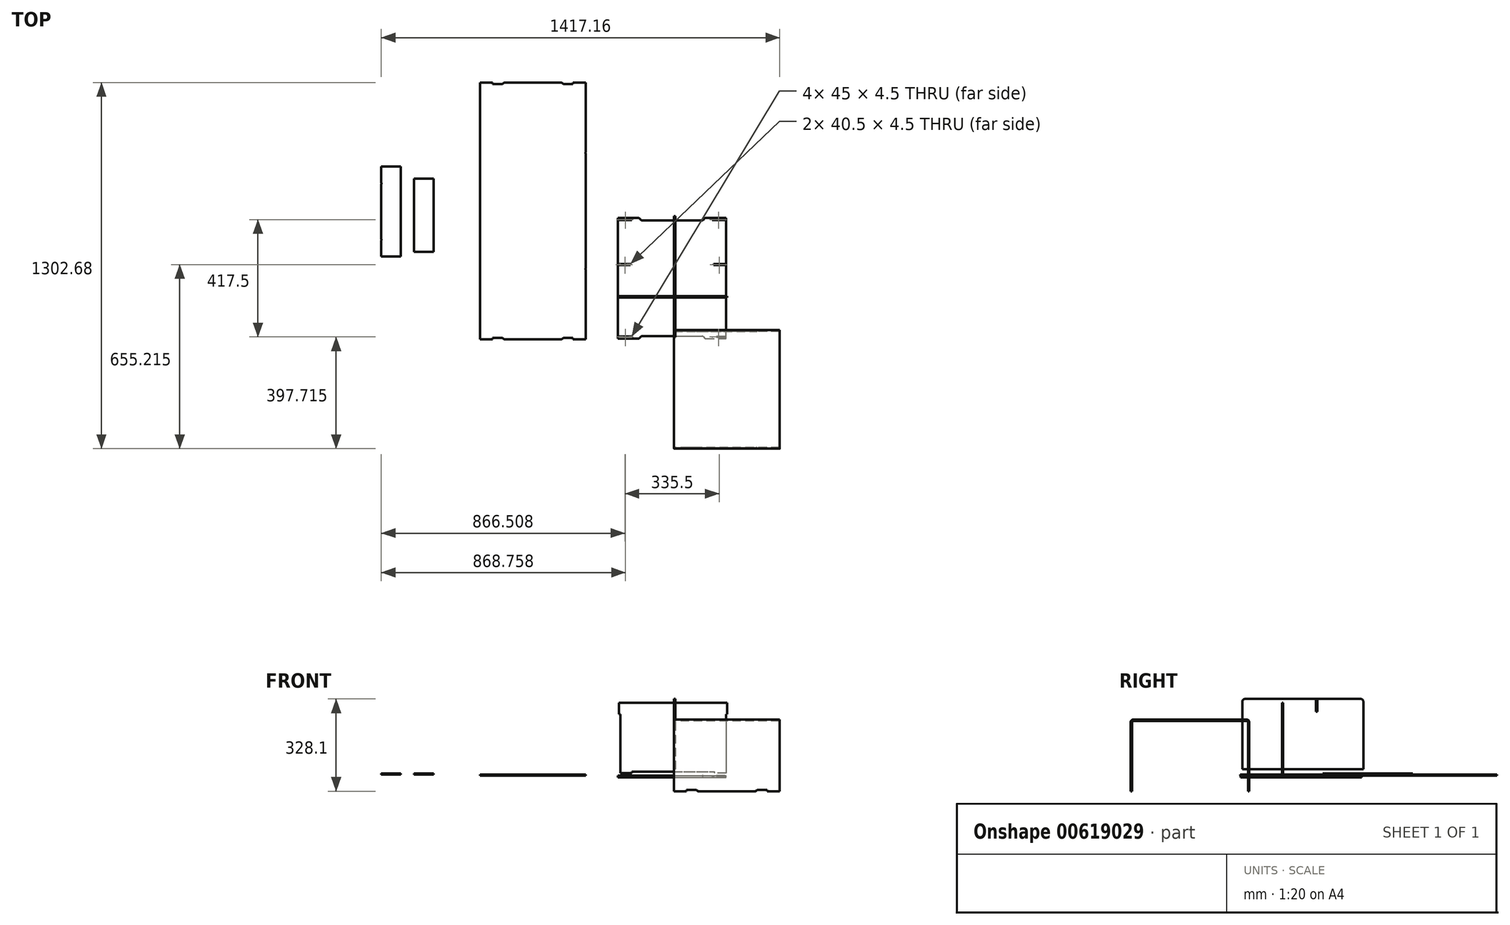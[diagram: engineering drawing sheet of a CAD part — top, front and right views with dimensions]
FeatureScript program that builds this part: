
annotation { "Feature Type Name" : "Feature", "Feature Type Description" : "" }
export const myFeature = defineFeature(function(context is Context, id is Id, definition is map)
    precondition{}
    {
        {
            var Q0;
            Q0=qCreatedBy(makeId("Top.planeOp"),FACE);
            var sketch = newSketch(context, id + "F0", { "sketchPlane" : qUnion([Q0])});
            skLineSegment(sketch, "E0.bottom", {"start": v(-199.4, -151.06) * mm, "end": v(-126.97, -151.06) * mm});
            skLineSegment(sketch, "E0.top", {"start": v(-199.4, 278.94) * mm, "end": v(-126.97, 278.94) * mm});
            skLineSegment(sketch, "E0.left", {"start": v(-199.4, -151.06) * mm, "end": v(-199.4, 110.44) * mm});
            skLineSegment(sketch, "E0.right", {"start": v(185.6, -151.06) * mm, "end": v(185.6, 110.44) * mm});
            skLineSegment(sketch, "E1", {"start": v(-194.9, 114.94) * mm, "end": v(-154.4, 114.94) * mm});
            skLineSegment(sketch, "E2", {"start": v(-154.4, 114.94) * mm, "end": v(-154.4, 110.44) * mm});
            skLineSegment(sketch, "E3", {"start": v(-154.4, 110.44) * mm, "end": v(-194.9, 110.44) * mm});
            skLineSegment(sketch, "E4", {"start": v(181.1, 114.94) * mm, "end": v(140.6, 114.94) * mm});
            skLineSegment(sketch, "E5", {"start": v(140.6, 114.94) * mm, "end": v(140.6, 110.44) * mm});
            skLineSegment(sketch, "E6", {"start": v(140.6, 110.44) * mm, "end": v(181.1, 110.44) * mm});
            skLineSegment(sketch, "E7.trimOffspring", {"start": v(-199.4, 114.94) * mm, "end": v(-199.4, 278.94) * mm});
            skLineSegment(sketch, "E8.trimOffspring", {"start": v(185.6, 114.94) * mm, "end": v(185.6, 278.94) * mm});
            skLineSegment(sketch, "E9", {"start": v(-199.4, 114.94) * mm, "end": v(-199.4, 110.44) * mm});
            skLineSegment(sketch, "E10", {"start": v(-194.9, 114.94) * mm, "end": v(-194.9, 110.44) * mm});
            skLineSegment(sketch, "E11", {"start": v(185.6, 114.94) * mm, "end": v(185.6, 110.44) * mm});
            skLineSegment(sketch, "E12", {"start": v(181.1, 114.94) * mm, "end": v(181.1, 110.44) * mm});
            skLineSegment(sketch, "E13.bottom", {"start": v(-194.9, -142.56) * mm, "end": v(-149.9, -142.56) * mm});
            skLineSegment(sketch, "E13.top", {"start": v(-194.9, -147.06) * mm, "end": v(-149.9, -147.06) * mm});
            skLineSegment(sketch, "E13.left", {"start": v(-194.9, -142.56) * mm, "end": v(-194.9, -147.06) * mm});
            skLineSegment(sketch, "E13.right", {"start": v(-149.9, -142.56) * mm, "end": v(-149.9, -147.06) * mm});
            skLineSegment(sketch, "E14.bottom", {"start": v(181.1, -142.56) * mm, "end": v(136.1, -142.56) * mm});
            skLineSegment(sketch, "E14.top", {"start": v(181.1, -147.06) * mm, "end": v(136.1, -147.06) * mm});
            skLineSegment(sketch, "E14.left", {"start": v(181.1, -142.56) * mm, "end": v(181.1, -147.06) * mm});
            skLineSegment(sketch, "E14.right", {"start": v(136.1, -142.56) * mm, "end": v(136.1, -147.06) * mm});
            skLineSegment(sketch, "E15.bottom", {"start": v(-194.9, 274.94) * mm, "end": v(-149.9, 274.94) * mm});
            skLineSegment(sketch, "E15.top", {"start": v(-194.9, 270.44) * mm, "end": v(-149.9, 270.44) * mm});
            skLineSegment(sketch, "E15.left", {"start": v(-194.9, 274.94) * mm, "end": v(-194.9, 270.44) * mm});
            skLineSegment(sketch, "E15.right", {"start": v(-149.9, 274.94) * mm, "end": v(-149.9, 270.44) * mm});
            skLineSegment(sketch, "E16.bottom", {"start": v(181.1, 274.94) * mm, "end": v(136.1, 274.94) * mm});
            skLineSegment(sketch, "E16.top", {"start": v(181.1, 270.44) * mm, "end": v(136.1, 270.44) * mm});
            skLineSegment(sketch, "E16.left", {"start": v(181.1, 274.94) * mm, "end": v(181.1, 270.44) * mm});
            skLineSegment(sketch, "E16.right", {"start": v(136.1, 274.94) * mm, "end": v(136.1, 270.44) * mm});
            skLineSegment(sketch, "E17", {"start": v(-123.44, 277.47) * mm, "end": v(-117.37, 271.4) * mm});
            skLineSegment(sketch, "E18", {"start": v(-113.83, 269.94) * mm, "end": v(100.03, 269.94) * mm});
            skLineSegment(sketch, "E19", {"start": v(103.56, 271.4) * mm, "end": v(109.63, 277.47) * mm});
            skLineSegment(sketch, "E20.trimOffspring", {"start": v(113.17, 278.94) * mm, "end": v(185.6, 278.94) * mm});
            skPoint(sketch, "E21.visualSharp", {"position": v(-124.9, 278.94) * mm});
            skArc(sketch, "E21.filletArc", {"start": v(-123.44, 277.47) * mm, "mid": v(-125.06, 278.55) * mm, "end": v(-126.97, 278.94) * mm});
            skPoint(sketch, "E22.visualSharp", {"position": v(-115.9, 269.94) * mm});
            skArc(sketch, "E22.filletArc", {"start": v(-117.37, 271.4) * mm, "mid": v(-115.74, 270.32) * mm, "end": v(-113.83, 269.94) * mm});
            skPoint(sketch, "E23.visualSharp", {"position": v(102.1, 269.94) * mm});
            skArc(sketch, "E23.filletArc", {"start": v(100.03, 269.94) * mm, "mid": v(101.94, 270.32) * mm, "end": v(103.56, 271.4) * mm});
            skPoint(sketch, "E24.visualSharp", {"position": v(111.1, 278.94) * mm});
            skArc(sketch, "E24.filletArc", {"start": v(113.17, 278.94) * mm, "mid": v(111.26, 278.55) * mm, "end": v(109.63, 277.47) * mm});
            skLineSegment(sketch, "E25", {"start": v(-123.44, -149.6) * mm, "end": v(-117.37, -143.53) * mm});
            skLineSegment(sketch, "E26", {"start": v(-113.83, -142.06) * mm, "end": v(100.03, -142.06) * mm});
            skLineSegment(sketch, "E27", {"start": v(103.56, -143.53) * mm, "end": v(109.63, -149.6) * mm});
            skLineSegment(sketch, "E28.trimOffspring", {"start": v(113.17, -151.06) * mm, "end": v(185.6, -151.06) * mm});
            skPoint(sketch, "E29.visualSharp", {"position": v(-124.9, -151.06) * mm});
            skArc(sketch, "E29.filletArc", {"start": v(-126.97, -151.06) * mm, "mid": v(-125.06, -150.68) * mm, "end": v(-123.44, -149.6) * mm});
            skPoint(sketch, "E30.visualSharp", {"position": v(-115.9, -142.06) * mm});
            skArc(sketch, "E30.filletArc", {"start": v(-113.83, -142.06) * mm, "mid": v(-115.74, -142.45) * mm, "end": v(-117.37, -143.53) * mm});
            skPoint(sketch, "E31.visualSharp", {"position": v(102.1, -142.06) * mm});
            skArc(sketch, "E31.filletArc", {"start": v(103.56, -143.53) * mm, "mid": v(101.94, -142.45) * mm, "end": v(100.03, -142.06) * mm});
            skPoint(sketch, "E32.visualSharp", {"position": v(111.1, -151.06) * mm});
            skArc(sketch, "E32.filletArc", {"start": v(109.63, -149.6) * mm, "mid": v(111.26, -150.68) * mm, "end": v(113.17, -151.06) * mm});
            skSolve(sketch);
        }
        {
            var Q0;
            Q0 = qSketchRegion(id + "F0", true);
            extrude(context, id + "F1", {"entities" : qUnion([Q0]), "depth" : 6 * mm, "offsetDistance" : 25 * mm});
        }
        {
            var Q0;
            Q0=qCreatedBy(makeId("Front.planeOp"),FACE);
            var sketch = newSketch(context, id + "F2", { "sketchPlane" : qUnion([Q0])});
            skLineSegment(sketch, "E33.bottom", {"start": v(-150.26, 20.88) * mm, "end": v(144.74, 20.88) * mm});
            skLineSegment(sketch, "E33.top", {"start": v(-190.76, 265.88) * mm, "end": v(185.24, 265.88) * mm});
            skLineSegment(sketch, "E33.left", {"start": v(-190.76, 20.88) * mm, "end": v(-190.76, 225.38) * mm});
            skLineSegment(sketch, "E33.right", {"start": v(185.24, 20.88) * mm, "end": v(185.24, 225.38) * mm});
            skLineSegment(sketch, "E34", {"start": v(-190.76, 20.88) * mm, "end": v(-190.76, 14.88) * mm});
            skLineSegment(sketch, "E35", {"start": v(-190.76, 14.88) * mm, "end": v(-150.26, 14.88) * mm});
            skLineSegment(sketch, "E36", {"start": v(-150.26, 14.88) * mm, "end": v(-150.26, 20.88) * mm});
            skLineSegment(sketch, "E37", {"start": v(185.24, 20.88) * mm, "end": v(185.24, 14.88) * mm});
            skLineSegment(sketch, "E38", {"start": v(185.24, 14.88) * mm, "end": v(144.74, 14.88) * mm});
            skLineSegment(sketch, "E39", {"start": v(144.74, 14.88) * mm, "end": v(144.74, 20.88) * mm});
            skLineSegment(sketch, "E40", {"start": v(-190.76, 265.88) * mm, "end": v(-195.26, 265.88) * mm});
            skLineSegment(sketch, "E41", {"start": v(-195.26, 265.88) * mm, "end": v(-195.26, 225.38) * mm});
            skLineSegment(sketch, "E42", {"start": v(-195.26, 225.38) * mm, "end": v(-190.76, 225.38) * mm});
            skLineSegment(sketch, "E43", {"start": v(185.24, 265.88) * mm, "end": v(189.74, 265.88) * mm});
            skLineSegment(sketch, "E44", {"start": v(189.74, 265.88) * mm, "end": v(189.74, 225.38) * mm});
            skLineSegment(sketch, "E45", {"start": v(189.74, 225.38) * mm, "end": v(185.24, 225.38) * mm});
            skSolve(sketch);
        }
        {
            var Q0;
            Q0 = qSketchRegion(id + "F2", true);
            extrude(context, id + "F3", {"entities" : qUnion([Q0]), "depth" : 4.5 * mm, "offsetDistance" : 25 * mm});
        }
        {
            var Q0;
            Q0=qCreatedBy(makeId("Right.planeOp"),FACE);
            var sketch = newSketch(context, id + "F4", { "sketchPlane" : qUnion([Q0])});
            skLineSegment(sketch, "E46.bottom", {"start": v(-145.05, 29.57) * mm, "end": v(284.95, 29.57) * mm});
            skLineSegment(sketch, "E46.top", {"start": v(-136.05, 279.07) * mm, "end": v(116.45, 279.07) * mm});
            skLineSegment(sketch, "E46.left", {"start": v(-145.05, 29.57) * mm, "end": v(-145.05, 270.07) * mm});
            skLineSegment(sketch, "E46.right", {"start": v(284.95, 29.57) * mm, "end": v(284.95, 270.07) * mm});
            skLineSegment(sketch, "E47", {"start": v(116.45, 274.57) * mm, "end": v(116.45, 234.07) * mm});
            skLineSegment(sketch, "E48", {"start": v(116.45, 234.07) * mm, "end": v(120.95, 234.07) * mm});
            skLineSegment(sketch, "E49", {"start": v(120.95, 234.07) * mm, "end": v(120.95, 274.57) * mm});
            skLineSegment(sketch, "E50.trimOffspring", {"start": v(120.95, 279.07) * mm, "end": v(275.95, 279.07) * mm});
            skLineSegment(sketch, "E51", {"start": v(116.45, 279.07) * mm, "end": v(120.95, 279.07) * mm});
            skLineSegment(sketch, "E52", {"start": v(116.45, 274.57) * mm, "end": v(120.95, 274.57) * mm});
            skPoint(sketch, "E53.visualSharp", {"position": v(-145.05, 279.07) * mm});
            skArc(sketch, "E53.filletArc", {"start": v(-136.05, 279.07) * mm, "mid": v(-142.42, 276.43) * mm, "end": v(-145.05, 270.07) * mm});
            skPoint(sketch, "E54.visualSharp", {"position": v(284.95, 279.07) * mm});
            skArc(sketch, "E54.filletArc", {"start": v(284.95, 270.07) * mm, "mid": v(282.31, 276.43) * mm, "end": v(275.95, 279.07) * mm});
            skSolve(sketch);
        }
        {
            var Q0;
            Q0 = qSketchRegion(id + "F4", true);
            extrude(context, id + "F5", {"entities" : qUnion([Q0]), "depth" : 4.5 * mm, "offsetDistance" : 25 * mm});
        }
        {
            var Q0;
            Q0=qCreatedBy(makeId("Right.planeOp"),FACE);
            var sketch = newSketch(context, id + "F6", { "sketchPlane" : qUnion([Q0])});
            skLineSegment(sketch, "E55.bottom", {"start": v(-120.53, -44.03) * mm, "end": v(-125.03, -44.03) * mm});
            skLineSegment(sketch, "E55.right", {"start": v(-542.53, -44.03) * mm, "end": v(-542.53, 196.47) * mm});
            skArc(sketch, "E56.filletArc", {"start": v(-533.53, 205.47) * mm, "mid": v(-539.9, 202.83) * mm, "end": v(-542.53, 196.47) * mm});
            skPoint(sketch, "E57.visualSharp", {"position": v(-120.53, 205.47) * mm});
            skLineSegment(sketch, "E58.top", {"start": v(-533.53, 200.97) * mm, "end": v(-129.53, 200.97) * mm});
            skLineSegment(sketch, "E58.left", {"start": v(-538.03, -44.03) * mm, "end": v(-538.03, 196.47) * mm});
            skLineSegment(sketch, "E58.right", {"start": v(-125.03, -44.03) * mm, "end": v(-125.03, 196.47) * mm});
            skLineSegment(sketch, "E59.trimOffspring", {"start": v(-538.03, -44.03) * mm, "end": v(-542.53, -44.03) * mm});
            skPoint(sketch, "E60.visualSharp", {"position": v(-538.03, 200.97) * mm});
            skArc(sketch, "E60.filletArc", {"start": v(-533.53, 200.97) * mm, "mid": v(-536.72, 199.65) * mm, "end": v(-538.03, 196.47) * mm});
            skLineSegment(sketch, "E61", {"start": v(-533.53, 205.47) * mm, "end": v(-129.53, 205.47) * mm});
            skLineSegment(sketch, "E62", {"start": v(-120.53, 196.47) * mm, "end": v(-120.53, -44.03) * mm});
            skPoint(sketch, "E63.visualSharp", {"position": v(-125.03, 200.97) * mm});
            skArc(sketch, "E63.filletArc", {"start": v(-125.03, 196.47) * mm, "mid": v(-126.35, 199.65) * mm, "end": v(-129.53, 200.97) * mm});
            skArc(sketch, "E64.filletArc", {"start": v(-120.53, 196.47) * mm, "mid": v(-123.17, 202.83) * mm, "end": v(-129.53, 205.47) * mm});
            skSolve(sketch);
        }
        {
            var Q0;
            Q0 = qSketchRegion(id + "F6", true);
            extrude(context, id + "F7", {"entities" : qUnion([Q0]), "depth" : 376 * mm, "offsetDistance" : 25 * mm});
        }
        {
            var Q0;
            Q0=makeQuery(id+"F7.opExtrude","SWEPT_FACE",FACE,{"disambiguationData":[OSD([sQuery(id+"F6.wireOp",EDGE,"E55.right")])]});
            var sketch = newSketch(context, id + "F8", { "sketchPlane" : qUnion([Q0])});
            skLineSegment(sketch, "E65", {"start": v(83.54, -47.57) * mm, "end": v(80, -44.03) * mm});
            skLineSegment(sketch, "E66", {"start": v(87.07, -49.03) * mm, "end": v(288.93, -49.03) * mm});
            skLineSegment(sketch, "E67", {"start": v(296, -44.03) * mm, "end": v(292.46, -47.57) * mm});
            skLineSegment(sketch, "E68", {"start": v(296, -44.03) * mm, "end": v(80, -44.03) * mm});
            skLineSegment(sketch, "E69.bottom", {"start": v(376, -44.03) * mm, "end": v(331, -44.03) * mm});
            skLineSegment(sketch, "E69.top", {"start": v(376, -49.03) * mm, "end": v(331, -49.03) * mm});
            skLineSegment(sketch, "E69.left", {"start": v(376, -44.03) * mm, "end": v(376, -49.03) * mm});
            skLineSegment(sketch, "E69.right", {"start": v(331, -44.03) * mm, "end": v(331, -49.03) * mm});
            skLineSegment(sketch, "E70.bottom", {"start": v(0, -44.03) * mm, "end": v(45, -44.03) * mm});
            skLineSegment(sketch, "E70.top", {"start": v(0, -49.03) * mm, "end": v(45, -49.03) * mm});
            skLineSegment(sketch, "E70.left", {"start": v(0, -44.03) * mm, "end": v(0, -49.03) * mm});
            skLineSegment(sketch, "E70.right", {"start": v(45, -44.03) * mm, "end": v(45, -49.03) * mm});
            skPoint(sketch, "E71.visualSharp", {"position": v(85, -49.03) * mm});
            skArc(sketch, "E71.filletArc", {"start": v(83.54, -47.57) * mm, "mid": v(85.16, -48.65) * mm, "end": v(87.07, -49.03) * mm});
            skPoint(sketch, "E72.visualSharp", {"position": v(291, -49.03) * mm});
            skArc(sketch, "E72.filletArc", {"start": v(288.93, -49.03) * mm, "mid": v(290.84, -48.65) * mm, "end": v(292.46, -47.57) * mm});
            skSolve(sketch);
        }
        {
            var Q0;
            Q0 = qSketchRegion(id + "F8", true);
            extrude(context, id + "F9", {"entities" : qUnion([Q0]), "operationType" : NewBodyOperationType.ADD, "oppositeDirection" : true, "depth" : 4.5 * mm, "offsetDistance" : 25 * mm});
        }
        {
            var Q0;
            Q0=makeQuery(id+"F7.opExtrude","SWEPT_FACE",FACE,{"disambiguationData":[OSD([sQuery(id+"F6.wireOp",EDGE,"E62")])]});
            var sketch = newSketch(context, id + "F10", { "sketchPlane" : qUnion([Q0])});
            skLineSegment(sketch, "E73.bottom", {"start": v(-376, -44.03) * mm, "end": v(-331, -44.03) * mm});
            skLineSegment(sketch, "E73.top", {"start": v(-376, -49.03) * mm, "end": v(-331, -49.03) * mm});
            skLineSegment(sketch, "E73.left", {"start": v(-376, -44.03) * mm, "end": v(-376, -49.03) * mm});
            skLineSegment(sketch, "E73.right", {"start": v(-331, -44.03) * mm, "end": v(-331, -49.03) * mm});
            skLineSegment(sketch, "E74.bottom", {"start": v(0, -44.03) * mm, "end": v(-45, -44.03) * mm});
            skLineSegment(sketch, "E74.top", {"start": v(0, -49.03) * mm, "end": v(-45, -49.03) * mm});
            skLineSegment(sketch, "E74.left", {"start": v(0, -44.03) * mm, "end": v(0, -49.03) * mm});
            skLineSegment(sketch, "E74.right", {"start": v(-45, -44.03) * mm, "end": v(-45, -49.03) * mm});
            skLineSegment(sketch, "E75", {"start": v(-296, -44.03) * mm, "end": v(-80, -44.03) * mm});
            skLineSegment(sketch, "E76", {"start": v(-80, -44.03) * mm, "end": v(-85, -49.03) * mm});
            skLineSegment(sketch, "E77", {"start": v(-85, -49.03) * mm, "end": v(-291, -49.03) * mm});
            skLineSegment(sketch, "E78", {"start": v(-291, -49.03) * mm, "end": v(-296, -44.03) * mm});
            skSolve(sketch);
        }
        {
            var Q0;
            Q0 = qSketchRegion(id + "F10", true);
            var Q1;
            {var subQ3=sQuery(id+"F10.wireOp",EDGE,"E73.bottom");Q1=makeQuery(id+"F10.imprint","IMPRINT",FACE,{"disambiguationData":[TD([[makeQuery(id+"F10.imprint","IMPRINT",EDGE,{"derivedFrom":subQ3}),1.0]])]});}
            extrude(context, id + "F11", {"entities" : qUnion([Q0, Q1]), "operationType" : NewBodyOperationType.ADD, "oppositeDirection" : true, "depth" : 4.5 * mm, "offsetDistance" : 25 * mm});
        }
        {
            var Q0;
            Q0=makeQuery(id+"F1.opExtrude","CAP_FACE",FACE,{"disambiguationData":[OSD([sQuery(id+"F0.wireOp",EDGE,"E0.bottom"),sQuery(id+"F0.wireOp",EDGE,"E0.top"),sQuery(id+"F0.wireOp",EDGE,"E0.left"),sQuery(id+"F0.wireOp",EDGE,"E0.right"),sQuery(id+"F0.wireOp",EDGE,"E1"),sQuery(id+"F0.wireOp",EDGE,"E2"),sQuery(id+"F0.wireOp",EDGE,"E3"),sQuery(id+"F0.wireOp",EDGE,"E4"),sQuery(id+"F0.wireOp",EDGE,"E5"),sQuery(id+"F0.wireOp",EDGE,"E6"),sQuery(id+"F0.wireOp",EDGE,"E7.trimOffspring"),sQuery(id+"F0.wireOp",EDGE,"E8.trimOffspring"),sQuery(id+"F0.wireOp",EDGE,"E9"),sQuery(id+"F0.wireOp",EDGE,"E10"),sQuery(id+"F0.wireOp",EDGE,"E11"),sQuery(id+"F0.wireOp",EDGE,"E12"),sQuery(id+"F0.wireOp",EDGE,"E13.bottom"),sQuery(id+"F0.wireOp",EDGE,"E13.top"),sQuery(id+"F0.wireOp",EDGE,"E13.left"),sQuery(id+"F0.wireOp",EDGE,"E13.right"),sQuery(id+"F0.wireOp",EDGE,"E14.bottom"),sQuery(id+"F0.wireOp",EDGE,"E14.top"),sQuery(id+"F0.wireOp",EDGE,"E14.left"),sQuery(id+"F0.wireOp",EDGE,"E14.right"),sQuery(id+"F0.wireOp",EDGE,"E15.bottom"),sQuery(id+"F0.wireOp",EDGE,"E15.top"),sQuery(id+"F0.wireOp",EDGE,"E15.left"),sQuery(id+"F0.wireOp",EDGE,"E15.right"),sQuery(id+"F0.wireOp",EDGE,"E16.bottom"),sQuery(id+"F0.wireOp",EDGE,"E16.top"),sQuery(id+"F0.wireOp",EDGE,"E16.left"),sQuery(id+"F0.wireOp",EDGE,"E16.right"),sQuery(id+"F0.wireOp",EDGE,"E17"),sQuery(id+"F0.wireOp",EDGE,"E18"),sQuery(id+"F0.wireOp",EDGE,"E19"),sQuery(id+"F0.wireOp",EDGE,"E20.trimOffspring"),sQuery(id+"F0.wireOp",EDGE,"E21.filletArc"),sQuery(id+"F0.wireOp",EDGE,"E22.filletArc"),sQuery(id+"F0.wireOp",EDGE,"E23.filletArc"),sQuery(id+"F0.wireOp",EDGE,"E24.filletArc"),sQuery(id+"F0.wireOp",EDGE,"E25"),sQuery(id+"F0.wireOp",EDGE,"E26"),sQuery(id+"F0.wireOp",EDGE,"E27"),sQuery(id+"F0.wireOp",EDGE,"E28.trimOffspring"),sQuery(id+"F0.wireOp",EDGE,"E29.filletArc"),sQuery(id+"F0.wireOp",EDGE,"E30.filletArc"),sQuery(id+"F0.wireOp",EDGE,"E31.filletArc"),sQuery(id+"F0.wireOp",EDGE,"E32.filletArc")])],"isStart":false});
            var sketch = newSketch(context, id + "F12", { "sketchPlane" : qUnion([Q0])});
            skLineSegment(sketch, "E79.top", {"start": v(-689.95, -152.85) * mm, "end": v(-644.95, -152.85) * mm});
            skLineSegment(sketch, "E79.right", {"start": v(-644.95, -147.85) * mm, "end": v(-644.95, -152.85) * mm});
            skLineSegment(sketch, "E80.top", {"start": v(-313.95, -152.85) * mm, "end": v(-358.95, -152.85) * mm});
            skLineSegment(sketch, "E80.right", {"start": v(-358.95, -147.85) * mm, "end": v(-358.95, -152.85) * mm});
            skLineSegment(sketch, "E81", {"start": v(-393.95, -147.85) * mm, "end": v(-398.95, -152.85) * mm});
            skLineSegment(sketch, "E82", {"start": v(-398.95, -152.85) * mm, "end": v(-604.95, -152.85) * mm});
            skLineSegment(sketch, "E83", {"start": v(-604.95, -152.85) * mm, "end": v(-609.95, -147.85) * mm});
            skLineSegment(sketch, "E84", {"start": v(-644.95, -147.85) * mm, "end": v(-609.95, -147.85) * mm});
            skLineSegment(sketch, "E85", {"start": v(-393.95, -147.85) * mm, "end": v(-358.95, -147.85) * mm});
            skLineSegment(sketch, "E86", {"start": v(-689.95, -152.85) * mm, "end": v(-689.95, 93.95) * mm});
            skLineSegment(sketch, "E87", {"start": v(-313.95, -152.85) * mm, "end": v(-313.95, 93.95) * mm});
            skLineSegment(sketch, "E88", {"start": v(-689.95, 760.15) * mm, "end": v(-644.95, 760.15) * mm});
            skLineSegment(sketch, "E89", {"start": v(-644.95, 760.15) * mm, "end": v(-644.95, 755.15) * mm});
            skLineSegment(sketch, "E90", {"start": v(-644.95, 755.15) * mm, "end": v(-609.95, 755.15) * mm});
            skLineSegment(sketch, "E91", {"start": v(-609.95, 755.15) * mm, "end": v(-604.95, 760.15) * mm});
            skLineSegment(sketch, "E92", {"start": v(-604.95, 760.15) * mm, "end": v(-398.95, 760.15) * mm});
            skLineSegment(sketch, "E93", {"start": v(-398.95, 760.15) * mm, "end": v(-393.95, 755.15) * mm});
            skLineSegment(sketch, "E94", {"start": v(-393.95, 755.15) * mm, "end": v(-358.95, 755.15) * mm});
            skLineSegment(sketch, "E95", {"start": v(-358.95, 755.15) * mm, "end": v(-358.95, 760.15) * mm});
            skLineSegment(sketch, "E96", {"start": v(-358.95, 760.15) * mm, "end": v(-313.95, 760.15) * mm});
            skLineSegment(sketch, "E97", {"start": v(-699.95, 804.6) * mm, "end": v(-699.95, -212.27) * mm, "construction": true});
            skLineSegment(sketch, "E98", {"start": v(-303.95, 800.48) * mm, "end": v(-303.95, -777.9) * mm, "construction": true});
            skArc(sketch, "E99", {"start": v(-689.95, 93.95) * mm, "mid": v(-689.45, 97.15) * mm, "end": v(-689.95, 100.35) * mm});
            skArc(sketch, "E100", {"start": v(-313.95, 513.35) * mm, "mid": v(-314.45, 510.15) * mm, "end": v(-313.95, 506.95) * mm});
            skArc(sketch, "E101", {"start": v(-313.95, 100.35) * mm, "mid": v(-314.45, 97.15) * mm, "end": v(-313.95, 93.95) * mm});
            skArc(sketch, "E102.trimOffspring", {"start": v(-689.95, 506.95) * mm, "mid": v(-689.45, 510.15) * mm, "end": v(-689.95, 513.35) * mm});
            skLineSegment(sketch, "E103.trimOffspring", {"start": v(-689.95, 513.35) * mm, "end": v(-689.95, 760.15) * mm});
            skLineSegment(sketch, "E104.trimOffspring", {"start": v(-313.95, 513.35) * mm, "end": v(-313.95, 760.15) * mm});
            skLineSegment(sketch, "E105.trimOffspring", {"start": v(-313.95, 100.35) * mm, "end": v(-313.95, 506.95) * mm});
            skLineSegment(sketch, "E106.trimOffspring", {"start": v(-689.95, 100.35) * mm, "end": v(-689.95, 506.95) * mm});
            skSolve(sketch);
        }
        {
            var Q0;
            Q0 = qSketchRegion(id + "F12", true);
            extrude(context, id + "F13", {"entities" : qUnion([Q0]), "depth" : 4.5 * mm, "offsetDistance" : 25 * mm});
        }
        {
            var Q0;
            Q0=makeQuery(id+"F13.opExtrude","CAP_FACE",FACE,{"disambiguationData":[OSD([sQuery(id+"F12.wireOp",EDGE,"E79.top"),sQuery(id+"F12.wireOp",EDGE,"E79.right"),sQuery(id+"F12.wireOp",EDGE,"E80.top"),sQuery(id+"F12.wireOp",EDGE,"E80.right"),sQuery(id+"F12.wireOp",EDGE,"E81"),sQuery(id+"F12.wireOp",EDGE,"E82"),sQuery(id+"F12.wireOp",EDGE,"E83"),sQuery(id+"F12.wireOp",EDGE,"E84"),sQuery(id+"F12.wireOp",EDGE,"E85"),sQuery(id+"F12.wireOp",EDGE,"E86"),sQuery(id+"F12.wireOp",EDGE,"E87"),sQuery(id+"F12.wireOp",EDGE,"E88"),sQuery(id+"F12.wireOp",EDGE,"E89"),sQuery(id+"F12.wireOp",EDGE,"E90"),sQuery(id+"F12.wireOp",EDGE,"E91"),sQuery(id+"F12.wireOp",EDGE,"E92"),sQuery(id+"F12.wireOp",EDGE,"E93"),sQuery(id+"F12.wireOp",EDGE,"E94"),sQuery(id+"F12.wireOp",EDGE,"E95"),sQuery(id+"F12.wireOp",EDGE,"E96"),sQuery(id+"F12.wireOp",EDGE,"E99"),sQuery(id+"F12.wireOp",EDGE,"E100"),sQuery(id+"F12.wireOp",EDGE,"E101"),sQuery(id+"F12.wireOp",EDGE,"E102.trimOffspring"),sQuery(id+"F12.wireOp",EDGE,"E103.trimOffspring"),sQuery(id+"F12.wireOp",EDGE,"E104.trimOffspring"),sQuery(id+"F12.wireOp",EDGE,"E105.trimOffspring"),sQuery(id+"F12.wireOp",EDGE,"E106.trimOffspring")])],"isStart":false});
            var sketch = newSketch(context, id + "F14", { "sketchPlane" : qUnion([Q0])});
            skLineSegment(sketch, "E107.bottom", {"start": v(-924.77, 417.7) * mm, "end": v(-854.77, 417.7) * mm});
            skLineSegment(sketch, "E107.top", {"start": v(-924.77, 157.7) * mm, "end": v(-854.77, 157.7) * mm});
            skLineSegment(sketch, "E107.left", {"start": v(-924.77, 417.7) * mm, "end": v(-924.77, 390.91) * mm});
            skLineSegment(sketch, "E107.right", {"start": v(-854.77, 417.7) * mm, "end": v(-854.77, 390.91) * mm});
            skLineSegment(sketch, "E108", {"start": v(-924.77, 387.7) * mm, "end": v(-854.77, 387.7) * mm, "construction": true});
            skLineSegment(sketch, "E109", {"start": v(-924.77, 187.7) * mm, "end": v(-854.77, 187.7) * mm, "construction": true});
            skLineSegment(sketch, "E110", {"start": v(-934.77, 433.06) * mm, "end": v(-934.77, 105.23) * mm, "construction": true});
            skLineSegment(sketch, "E111", {"start": v(-844.77, 435.15) * mm, "end": v(-844.77, 87.48) * mm, "construction": true});
            skArc(sketch, "E112", {"start": v(-854.77, 390.91) * mm, "mid": v(-855.27, 387.7) * mm, "end": v(-854.77, 384.5) * mm});
            skArc(sketch, "E113", {"start": v(-854.77, 190.91) * mm, "mid": v(-855.27, 187.7) * mm, "end": v(-854.77, 184.5) * mm});
            skArc(sketch, "E114", {"start": v(-924.77, 184.5) * mm, "mid": v(-924.27, 187.7) * mm, "end": v(-924.77, 190.91) * mm});
            skLineSegment(sketch, "E115.trimOffspring", {"start": v(-924.77, 184.5) * mm, "end": v(-924.77, 157.7) * mm});
            skLineSegment(sketch, "E116.trimOffspring", {"start": v(-854.77, 184.5) * mm, "end": v(-854.77, 157.7) * mm});
            skLineSegment(sketch, "E117.trimOffspring", {"start": v(-854.77, 384.5) * mm, "end": v(-854.77, 190.91) * mm});
            skLineSegment(sketch, "E118.trimOffspring", {"start": v(-924.77, 384.5) * mm, "end": v(-924.77, 190.91) * mm});
            skArc(sketch, "E119.trimOffspring", {"start": v(-924.77, 384.5) * mm, "mid": v(-924.27, 387.7) * mm, "end": v(-924.77, 390.91) * mm});
            skSolve(sketch);
        }
        {
            var Q0;
            Q0 = qSketchRegion(id + "F14", true);
            extrude(context, id + "F15", {"entities" : qUnion([Q0]), "depth" : 3 * mm, "offsetDistance" : 25 * mm});
        }
        {
            var Q0;
            Q0=makeQuery(id+"F13.opExtrude","CAP_FACE",FACE,{"disambiguationData":[OSD([sQuery(id+"F12.wireOp",EDGE,"E79.top"),sQuery(id+"F12.wireOp",EDGE,"E79.right"),sQuery(id+"F12.wireOp",EDGE,"E80.top"),sQuery(id+"F12.wireOp",EDGE,"E80.right"),sQuery(id+"F12.wireOp",EDGE,"E81"),sQuery(id+"F12.wireOp",EDGE,"E82"),sQuery(id+"F12.wireOp",EDGE,"E83"),sQuery(id+"F12.wireOp",EDGE,"E84"),sQuery(id+"F12.wireOp",EDGE,"E85"),sQuery(id+"F12.wireOp",EDGE,"E86"),sQuery(id+"F12.wireOp",EDGE,"E87"),sQuery(id+"F12.wireOp",EDGE,"E88"),sQuery(id+"F12.wireOp",EDGE,"E89"),sQuery(id+"F12.wireOp",EDGE,"E90"),sQuery(id+"F12.wireOp",EDGE,"E91"),sQuery(id+"F12.wireOp",EDGE,"E92"),sQuery(id+"F12.wireOp",EDGE,"E93"),sQuery(id+"F12.wireOp",EDGE,"E94"),sQuery(id+"F12.wireOp",EDGE,"E95"),sQuery(id+"F12.wireOp",EDGE,"E96"),sQuery(id+"F12.wireOp",EDGE,"E99"),sQuery(id+"F12.wireOp",EDGE,"E100"),sQuery(id+"F12.wireOp",EDGE,"E101"),sQuery(id+"F12.wireOp",EDGE,"E102.trimOffspring"),sQuery(id+"F12.wireOp",EDGE,"E103.trimOffspring"),sQuery(id+"F12.wireOp",EDGE,"E104.trimOffspring"),sQuery(id+"F12.wireOp",EDGE,"E105.trimOffspring"),sQuery(id+"F12.wireOp",EDGE,"E106.trimOffspring")])],"isStart":false});
            var sketch = newSketch(context, id + "F16", { "sketchPlane" : qUnion([Q0])});
            skLineSegment(sketch, "E120.bottom", {"start": v(-1041.16, 460.88) * mm, "end": v(-971.16, 460.88) * mm});
            skLineSegment(sketch, "E120.top", {"start": v(-1041.16, 140.88) * mm, "end": v(-971.16, 140.88) * mm});
            skLineSegment(sketch, "E120.left", {"start": v(-1041.16, 460.88) * mm, "end": v(-1041.16, 404.08) * mm});
            skLineSegment(sketch, "E120.right", {"start": v(-971.16, 460.88) * mm, "end": v(-971.16, 404.08) * mm});
            skLineSegment(sketch, "E121", {"start": v(-1041.16, 400.88) * mm, "end": v(-971.16, 400.88) * mm, "construction": true});
            skLineSegment(sketch, "E122", {"start": v(-1041.16, 200.88) * mm, "end": v(-971.16, 200.88) * mm, "construction": true});
            skLineSegment(sketch, "E123", {"start": v(-1051.16, 446.23) * mm, "end": v(-1051.16, 118.4) * mm, "construction": true});
            skLineSegment(sketch, "E124", {"start": v(-961.16, 448.32) * mm, "end": v(-961.16, 100.65) * mm, "construction": true});
            skArc(sketch, "E125", {"start": v(-971.16, 404.08) * mm, "mid": v(-971.66, 400.88) * mm, "end": v(-971.16, 397.68) * mm});
            skArc(sketch, "E126", {"start": v(-971.16, 204.08) * mm, "mid": v(-971.66, 200.88) * mm, "end": v(-971.16, 197.68) * mm});
            skArc(sketch, "E127", {"start": v(-1041.16, 197.68) * mm, "mid": v(-1040.66, 200.88) * mm, "end": v(-1041.16, 204.08) * mm});
            skLineSegment(sketch, "E128.trimOffspring", {"start": v(-1041.16, 197.68) * mm, "end": v(-1041.16, 140.88) * mm});
            skLineSegment(sketch, "E129.trimOffspring", {"start": v(-971.16, 197.68) * mm, "end": v(-971.16, 140.88) * mm});
            skLineSegment(sketch, "E130.trimOffspring", {"start": v(-971.16, 397.68) * mm, "end": v(-971.16, 204.08) * mm});
            skLineSegment(sketch, "E131.trimOffspring", {"start": v(-1041.16, 397.68) * mm, "end": v(-1041.16, 204.08) * mm});
            skArc(sketch, "E132.trimOffspring", {"start": v(-1041.16, 397.68) * mm, "mid": v(-1040.66, 400.88) * mm, "end": v(-1041.16, 404.08) * mm});
            skSolve(sketch);
        }
        {
            var Q0;
            Q0 = qSketchRegion(id + "F16", true);
            extrude(context, id + "F17", {"entities" : qUnion([Q0]), "depth" : 3 * mm, "offsetDistance" : 25 * mm});
        }
    });
